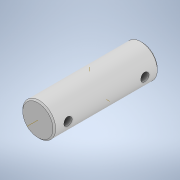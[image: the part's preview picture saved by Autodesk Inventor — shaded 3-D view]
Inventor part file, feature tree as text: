
AUTODESK INVENTOR PART (.ipt)
format: ipt  version: 2021.1 (Build 251245000, 245)  size: 126,976 bytes
history: native  units: in
note: dims shown in document units (in); Inventor stores cm internally (conversion verified against a paired STEP export)
features: extrude x2, sketch x2, projected_geometry x2, chamfer x1
ambient origin geometry x8: Origin, YZ Plane, XZ Plane, XY Plane, X Axis, Y Axis, Z Axis, Center Point
bodies: Solid1 (feature_tree)
feature tree (7):
  extrude  "Extrusion1"  Depth=3.8in TaperAngle=0.0deg
  extrude  "Extrusion2"  Depth=0.3in
  chamfer  "Chamfer1"  Distance=0.5in
  sketch  "Sketch1"  dims[d0=1.2in d1=3.8in d2=0.0in]
  sketch  "Sketch2"  dims[d3=0.3in d4=0.3in d5=0.5in d6=0.5in d7=0.0in d8=0.0in d9=0.05in d10=0.125in d11=45.0deg]
  projected_geometry  "Projected Loop1"
  projected_geometry  "Project Cut Edges1"
